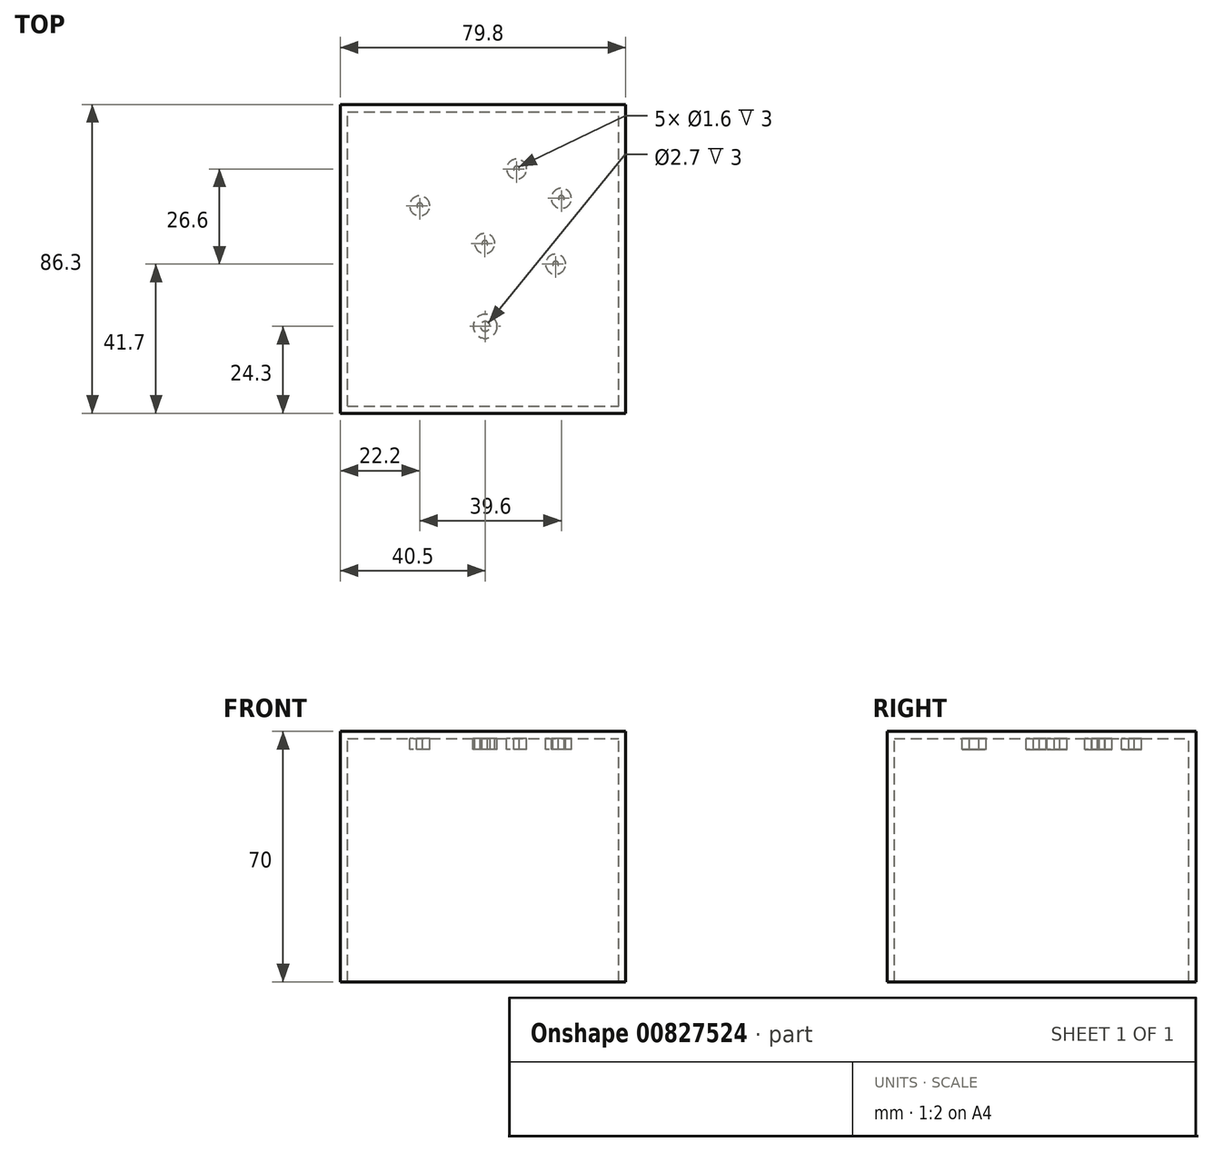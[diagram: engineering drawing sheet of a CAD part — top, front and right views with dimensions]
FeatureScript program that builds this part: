
annotation { "Feature Type Name" : "Feature", "Feature Type Description" : "" }
export const myFeature = defineFeature(function(context is Context, id is Id, definition is map)
    precondition{}
    {
        {
            var Q0;
            Q0=qCreatedBy(makeId("Top.planeOp"),FACE);
            var sketch = newSketch(context, id + "F0", { "sketchPlane" : qUnion([Q0])});
            skCircle(sketch, "E0", {"center": v(4.2, 40) * mm, "radius": 0.8 * mm});
            skCircle(sketch, "E1", {"center": v(31.3, 50.3) * mm, "radius": 0.8 * mm});
            skCircle(sketch, "E2", {"center": v(43.8, 42.1) * mm, "radius": 0.8 * mm});
            skCircle(sketch, "E3", {"center": v(22.4, 29.5) * mm, "radius": 0.8 * mm});
            skCircle(sketch, "E4", {"center": v(22.5, 6.3) * mm, "radius": 1.35 * mm});
            skCircle(sketch, "E5", {"center": v(42.2, 23.7) * mm, "radius": 0.8 * mm});
            skSolve(sketch);
        }
        {
            var Q0;
            Q0=qCreatedBy(makeId("Top.planeOp"),FACE);
            var sketch = newSketch(context, id + "F1", { "sketchPlane" : qUnion([Q0])});
            skLineSegment(sketch, "E6.bottom", {"start": v(-16, -16) * mm, "end": v(59.8, -16) * mm});
            skLineSegment(sketch, "E6.top", {"start": v(-16, 66.3) * mm, "end": v(59.8, 66.3) * mm});
            skLineSegment(sketch, "E6.left", {"start": v(-16, -16) * mm, "end": v(-16, 66.3) * mm});
            skLineSegment(sketch, "E6.right", {"start": v(59.8, -16) * mm, "end": v(59.8, 66.3) * mm});
            skLineSegment(sketch, "E7.bottom", {"start": v(-18, -18) * mm, "end": v(61.8, -18) * mm});
            skLineSegment(sketch, "E7.top", {"start": v(-18, 68.3) * mm, "end": v(61.8, 68.3) * mm});
            skLineSegment(sketch, "E7.left", {"start": v(-18, -18) * mm, "end": v(-18, 68.3) * mm});
            skLineSegment(sketch, "E7.right", {"start": v(61.8, -18) * mm, "end": v(61.8, 68.3) * mm});
            skSolve(sketch);
        }
        {
            var Q0;
            Q0 = qSketchRegion(id + "F1", true);
            extrude(context, id + "F2", {"entities" : qUnion([Q0]), "oppositeDirection" : true, "depth" : 70 * mm, "offsetDistance" : 25 * mm});
        }
        {
            var Q0;
            Q0=makeQuery(id+"F1.imprint","IMPRINT",FACE,{"disambiguationData":[TD([[makeQuery(id+"F1.imprint","IMPRINT",EDGE,{"derivedFrom":sQuery(id+"F1.wireOp",EDGE,"E6.bottom")}),1.0]])]});
            extrude(context, id + "F3", {"entities" : qUnion([Q0]), "operationType" : NewBodyOperationType.ADD, "oppositeDirection" : true, "depth" : 2 * mm, "offsetDistance" : 25 * mm});
        }
        {
            var Q0;
            Q0=qCreatedBy(makeId("Top.planeOp"),FACE);
            var sketch = newSketch(context, id + "F4", { "sketchPlane" : qUnion([Q0])});
            skCircle(sketch, "E8", {"center": v(22.5, 6.3) * mm, "radius": 3.35 * mm});
            skCircle(sketch, "E9.0", {"center": v(22.5, 6.3) * mm, "radius": 1.35 * mm});
            skCircle(sketch, "E10.0", {"center": v(22.4, 29.5) * mm, "radius": 0.8 * mm});
            skCircle(sketch, "E11.0", {"center": v(42.2, 23.7) * mm, "radius": 0.8 * mm});
            skPoint(sketch, "E12.0", {"position": v(43.8, 42.1) * mm});
            skCircle(sketch, "E13.0", {"center": v(43.8, 42.1) * mm, "radius": 0.8 * mm});
            skCircle(sketch, "E14.0", {"center": v(4.2, 40) * mm, "radius": 0.8 * mm});
            skPoint(sketch, "E15.0", {"position": v(31.3, 50.3) * mm});
            skCircle(sketch, "E16.0", {"center": v(31.3, 50.3) * mm, "radius": 0.8 * mm});
            skCircle(sketch, "E17", {"center": v(42.2, 23.7) * mm, "radius": 2.8 * mm});
            skCircle(sketch, "E18", {"center": v(22.4, 29.5) * mm, "radius": 2.8 * mm});
            skCircle(sketch, "E19", {"center": v(4.2, 40) * mm, "radius": 2.8 * mm});
            skCircle(sketch, "E20", {"center": v(43.8, 42.1) * mm, "radius": 2.8 * mm});
            skCircle(sketch, "E21", {"center": v(31.3, 50.3) * mm, "radius": 2.8 * mm});
            skSolve(sketch);
        }
        {
            var Q0;
            Q0 = qSketchRegion(id + "F4", true);
            extrude(context, id + "F5", {"entities" : qUnion([Q0]), "operationType" : NewBodyOperationType.ADD, "oppositeDirection" : true, "depth" : 5 * mm, "offsetDistance" : 25 * mm});
        }
    });
